# Revit family: UB with 2dstud
name_source: partatom
category: Structural Framing
revit_build: Autodesk Revit Structure 2012 (Build: 20110309_2315)
units: mm (PartAtom-declared; Revit-internal decimal feet)

## types (5) — shared parameters
Type Comments = Steel 43-275

## per-type parameters (varying)
| type | A | W | bf | d | k | kr | tf | tw |
| UB305x127x37 | 0 m² | 0.037 | 124 mm | 304 mm | 20 mm | 9 mm  [stored 0.0295276 ft] | 11 mm | 7 mm  [stored 0.0229659 ft] |
| UB305x102x25 | 0 m² | 0.0248 | 102 mm | 305 mm | 14 mm  [stored 0.0459318 ft] | 8 mm  [stored 0.0262467 ft] | 7 mm  [stored 0.0229659 ft] | 6 mm  [stored 0.019685 ft] |
| UB838x292x226 | 0.03 m² | 0.2265 | 294 mm | 851 mm | 45 mm | 18 mm  [stored 0.0590551 ft] | 27 mm | 16 mm |
| UB457x152x67 | 0.01 m² | 0.0672 | 152 mm | 457 mm | 25 mm  [stored 0.082021 ft] | 10 mm  [stored 0.0328084 ft] | 15 mm  [stored 0.0492126 ft] | 9 mm  [stored 0.0295276 ft] |
| UB127x76x13 | 0 m² | 0.013 | 76 mm | 127 mm | 15 mm  [stored 0.0492126 ft] | 8 mm  [stored 0.0262467 ft] | 8 mm  [stored 0.0262467 ft] | 4 mm  [stored 0.0131234 ft] |

note: [stored X ft] marks values corroborated as IEEE doubles in the binary element streams (Revit-internal decimal feet)

## geometry (parser evidence)
native form markers: Sweep x5
no freeform markers — native parametric forms only
